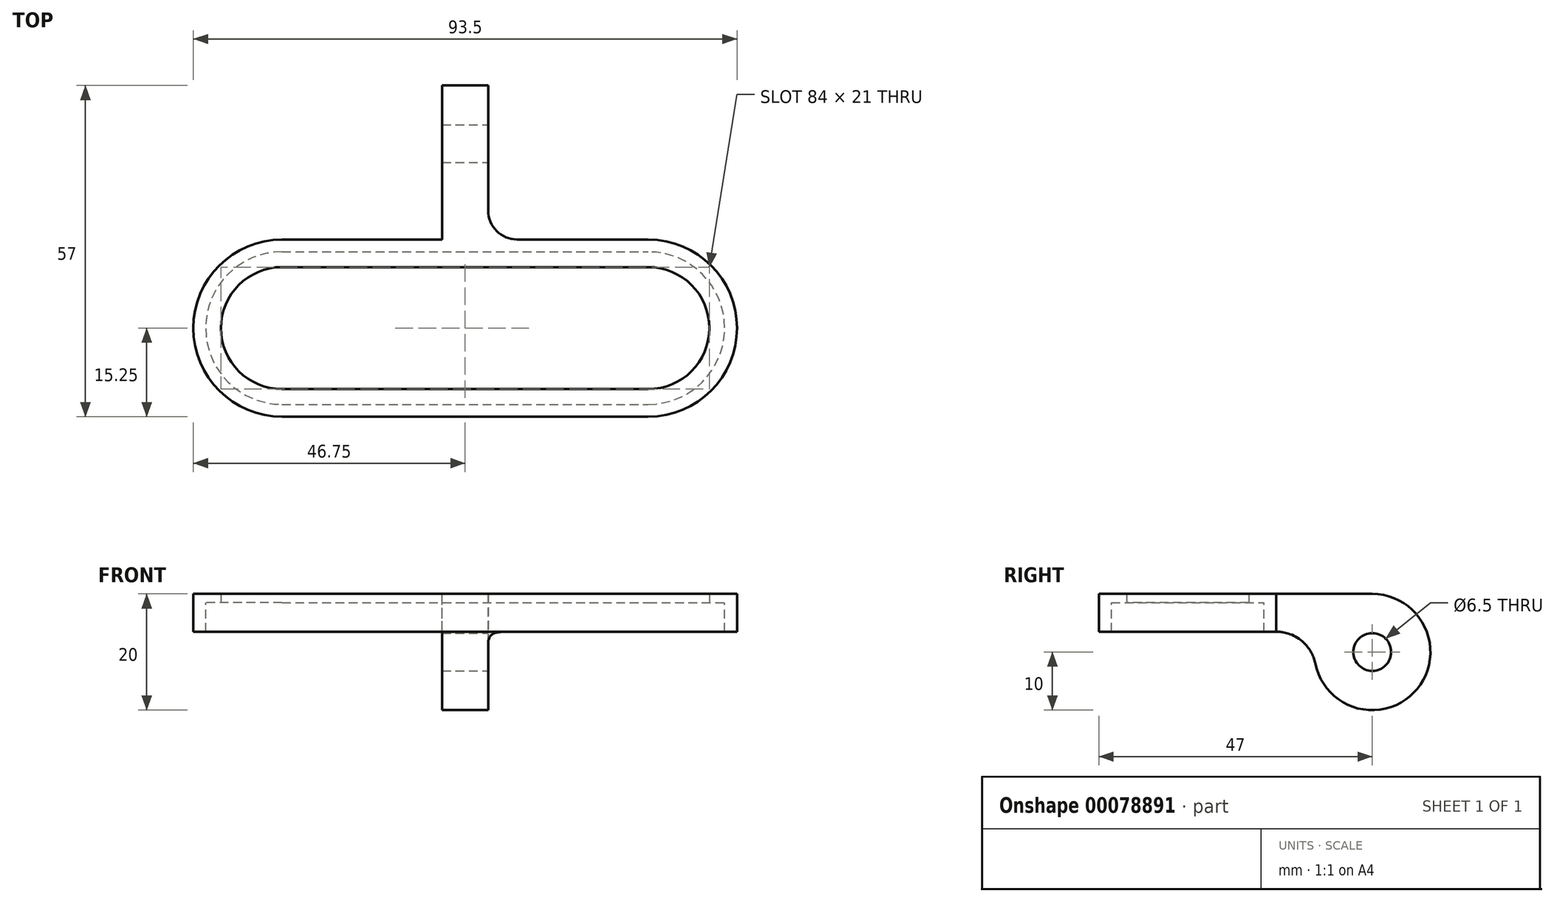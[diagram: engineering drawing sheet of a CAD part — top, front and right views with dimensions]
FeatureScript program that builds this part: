
annotation { "Feature Type Name" : "Feature", "Feature Type Description" : "" }
export const myFeature = defineFeature(function(context is Context, id is Id, definition is map)
    precondition{}
    {
        {
            var Q0;
            Q0=qCreatedBy(makeId("Top.planeOp"),FACE);
            var sketch = newSketch(context, id + "F0", { "sketchPlane" : qUnion([Q0])});
            skLineSegment(sketch, "E0", {"start": v(0, 0) * mm, "end": v(63, 0) * mm, "construction": true});
            skLineSegment(sketch, "E1", {"start": v(0, -25.5) * mm, "end": v(63, -25.5) * mm, "construction": true});
            skArc(sketch, "E2", {"start": v(0, -25.5) * mm, "mid": v(-12.75, -12.75) * mm, "end": v(0, 0) * mm, "construction": true});
            skArc(sketch, "E3", {"start": v(63, 0) * mm, "mid": v(75.75, -12.75) * mm, "end": v(63, -25.5) * mm, "construction": true});
            skArc(sketch, "E4.0", {"start": v(0, -23.25) * mm, "mid": v(-10.5, -12.75) * mm, "end": v(0, -2.25) * mm});
            skLineSegment(sketch, "E4.1", {"start": v(0, -23.25) * mm, "end": v(63, -23.25) * mm});
            skArc(sketch, "E4.2", {"start": v(63, -2.25) * mm, "mid": v(73.5, -12.75) * mm, "end": v(63, -23.25) * mm});
            skLineSegment(sketch, "E4.3", {"start": v(0, -2.25) * mm, "end": v(63, -2.25) * mm});
            skArc(sketch, "E5.0", {"start": v(0, -28) * mm, "mid": v(-15.25, -12.75) * mm, "end": v(0, 2.5) * mm});
            skLineSegment(sketch, "E5.1", {"start": v(0, -28) * mm, "end": v(63, -28) * mm});
            skArc(sketch, "E5.2", {"start": v(63, 2.5) * mm, "mid": v(78.25, -12.75) * mm, "end": v(63, -28) * mm});
            skLineSegment(sketch, "E5.3", {"start": v(0, 2.5) * mm, "end": v(63, 2.5) * mm});
            skSolve(sketch);
        }
        {
            var Q0;
            Q0 = qSketchRegion(id + "F0", true);
            extrude(context, id + "F1", {"entities" : qUnion([Q0]), "depth" : 1.5 * mm});
        }
        {
            var Q0;
            Q0=makeQuery(id+"F1.opExtrude","CAP_FACE",FACE,{"disambiguationData":[OSD([sQuery(id+"F0.wireOp",EDGE,"E4.0"),sQuery(id+"F0.wireOp",EDGE,"E4.1"),sQuery(id+"F0.wireOp",EDGE,"E4.2"),sQuery(id+"F0.wireOp",EDGE,"E4.3"),sQuery(id+"F0.wireOp",EDGE,"E5.0"),sQuery(id+"F0.wireOp",EDGE,"E5.1"),sQuery(id+"F0.wireOp",EDGE,"E5.2"),sQuery(id+"F0.wireOp",EDGE,"E5.3")])],"isStart":true});
            var sketch = newSketch(context, id + "F2", { "sketchPlane" : qUnion([Q0])});
            skArc(sketch, "E6.0", {"start": v(0, 25.88) * mm, "mid": v(-13.13, 12.75) * mm, "end": v(0, -0.38) * mm});
            skLineSegment(sketch, "E6.1", {"start": v(0, 25.88) * mm, "end": v(63, 25.88) * mm});
            skArc(sketch, "E6.2", {"start": v(63, -0.38) * mm, "mid": v(76.12, 12.75) * mm, "end": v(63, 25.88) * mm});
            skLineSegment(sketch, "E6.3", {"start": v(0, -0.38) * mm, "end": v(63, -0.38) * mm});
            skLineSegment(sketch, "E7", {"start": v(0, 28) * mm, "end": v(63, 28) * mm});
            skLineSegment(sketch, "E8", {"start": v(0, -2.5) * mm, "end": v(63, -2.5) * mm});
            skArc(sketch, "E9", {"start": v(63, 28) * mm, "mid": v(78.25, 12.75) * mm, "end": v(63, -2.5) * mm});
            skArc(sketch, "E10", {"start": v(0, 28) * mm, "mid": v(-15.25, 12.75) * mm, "end": v(0, -2.5) * mm});
            skSolve(sketch);
        }
        {
            var Q0;
            Q0 = qSketchRegion(id + "F2", true);
            extrude(context, id + "F3", {"entities" : qUnion([Q0]), "operationType" : NewBodyOperationType.ADD, "depth" : 5 * mm});
        }
        {
            var Q0;
            Q0=makeQuery(id+"F3.boolean.opBoolean","MERGE",FACE,{"derivedFrom":[makeQuery(id+"F1.opExtrude","SWEPT_FACE",FACE,{"disambiguationData":[OSD([sQuery(id+"F0.wireOp",EDGE,"E5.3")])]}),makeQuery(id+"F3.opExtrude","SWEPT_FACE",FACE,{"disambiguationData":[OSD([sQuery(id+"F2.wireOp",EDGE,"E8")])]})]});
            var sketch = newSketch(context, id + "F4", { "sketchPlane" : qUnion([Q0])});
            skLineSegment(sketch, "E11", {"start": v(-31.5, -18.5) * mm, "end": v(-31.5, 1.5) * mm, "construction": true});
            skPoint(sketch, "E11.endSnap0", {"position": v(-31.5, 1.5) * mm});
            skLineSegment(sketch, "E12", {"start": v(-27.55, -18.5) * mm, "end": v(-27.55, 1.5) * mm});
            skLineSegment(sketch, "E13", {"start": v(-27.55, 1.5) * mm, "end": v(-35.45, 1.5) * mm});
            skLineSegment(sketch, "E14", {"start": v(-35.45, 1.5) * mm, "end": v(-35.45, -18.5) * mm});
            skLineSegment(sketch, "E15", {"start": v(-35.45, -18.5) * mm, "end": v(-27.55, -18.5) * mm});
            skLineSegment(sketch, "E16", {"start": v(0, -1.75) * mm, "end": v(-63, -1.75) * mm, "construction": true});
            skLineSegment(sketch, "E17", {"start": v(-27.55, -8.5) * mm, "end": v(-35.45, -8.5) * mm, "construction": true});
            skSolve(sketch);
        }
        {
            var Q0;
            Q0 = qSketchRegion(id + "F4", true);
            extrude(context, id + "F5", {"entities" : qUnion([Q0]), "operationType" : NewBodyOperationType.ADD, "depth" : 26.5 * mm});
        }
        {
            var Q0;
            Q0=makeQuery(id+"F5.opExtrude","SWEPT_FACE",FACE,{"disambiguationData":[OSD([sQuery(id+"F4.wireOp",EDGE,"E14")])]});
            var sketch = newSketch(context, id + "F6", { "sketchPlane" : qUnion([Q0])});
            skLineSegment(sketch, "E18", {"start": v(2.5, -5) * mm, "end": v(0.38, -5) * mm});
            skLineSegment(sketch, "E19", {"start": v(2.5, -5) * mm, "end": v(2.5, -7.12) * mm});
            skArc(sketch, "E20", {"start": v(2.5, -7.12) * mm, "mid": v(1.88, -5.62) * mm, "end": v(0.38, -5) * mm});
            skSolve(sketch);
        }
        {
            var Q0;
            Q0=makeQuery(id+"FXbGKdrpCwlS0YJ_1.boolean.opBoolean","MERGE",FACE,{"derivedFrom":[makeQuery(id+"F5.opExtrude","SWEPT_FACE",FACE,{"disambiguationData":[OSD([sQuery(id+"F4.wireOp",EDGE,"E14")])]}),makeQuery(id+"FXbGKdrpCwlS0YJ_1.opExtrude","CAP_FACE",FACE,{"disambiguationData":[OSD([sQuery(id+"F6.wireOp",EDGE,"E18"),sQuery(id+"F6.wireOp",EDGE,"E19"),sQuery(id+"F6.wireOp",EDGE,"E20")])],"isStart":true})]});
            var sketch = newSketch(context, id + "F7", { "sketchPlane" : qUnion([Q0])});
            skLineSegment(sketch, "E21", {"start": v(29, -18.5) * mm, "end": v(19, -18.5) * mm, "construction": true});
            skLineSegment(sketch, "E22", {"start": v(29, -8.5) * mm, "end": v(41.92, -8.5) * mm, "construction": true});
            skLineSegment(sketch, "E23", {"start": v(29, -8.5) * mm, "end": v(29, -18.5) * mm, "construction": true});
            skLineSegment(sketch, "E24", {"start": v(29, -8.5) * mm, "end": v(29, 1.5) * mm, "construction": true});
            skLineSegment(sketch, "E25", {"start": v(29, 1.5) * mm, "end": v(19, 1.5) * mm, "construction": true});
            skLineSegment(sketch, "E26", {"start": v(-1.5, -23.8) * mm, "end": v(36.26, -23.8) * mm});
            skLineSegment(sketch, "E27", {"start": v(36.26, -23.8) * mm, "end": v(36.26, 7.74) * mm});
            skLineSegment(sketch, "E28", {"start": v(36.26, 7.74) * mm, "end": v(19, 7.74) * mm});
            skLineSegment(sketch, "E29", {"start": v(19, 7.74) * mm, "end": v(19, 1.5) * mm});
            skArc(sketch, "E30", {"start": v(19, -18.5) * mm, "mid": v(29, -8.5) * mm, "end": v(19, 1.5) * mm});
            skCircle(sketch, "E31", {"center": v(19, -8.5) * mm, "radius": 3.25 * mm});
            skArc(sketch, "E32", {"start": v(19, -18.5) * mm, "mid": v(12.67, -16.24) * mm, "end": v(9.2, -10.48) * mm});
            skArc(sketch, "E33", {"start": v(9.2, -10.48) * mm, "mid": v(6.83, -6.54) * mm, "end": v(2.5, -5) * mm});
            skLineSegment(sketch, "E34", {"start": v(-1.5, -23.8) * mm, "end": v(-1.5, -8.44) * mm});
            skLineSegment(sketch, "E35", {"start": v(-1.5, -8.44) * mm, "end": v(2.5, -5) * mm});
            skSolve(sketch);
        }
        {
            var Q0;
            Q0 = qSketchRegion(id + "F7", true);
            extrude(context, id + "F8", {"entities" : qUnion([Q0]), "operationType" : NewBodyOperationType.REMOVE, "endBound" : BoundingType.THROUGH_ALL, "oppositeDirection" : true, "depth" : 25 * mm});
        }
        {
            var Q0;
            {var subQ1=sQuery(id+"F4.wireOp",EDGE,"E13");var subQ3=sQuery(id+"F4.wireOp",EDGE,"E14");Q0=makeQuery(id+"F5.boolean.opBoolean","SPLIT",EDGE,{"disambiguationData":[TD([makeQuery(id+"F5.opExtrude","SWEPT_FACE",FACE,{"disambiguationData":[OSD([subQ1])]})])],"derivedFrom":makeQuery(id+"F5.opExtrude","CAP_EDGE",EDGE,{"disambiguationData":[OSD([subQ3])],"isStart":true})});}
            var Q1;
            {var subQ1=sQuery(id+"F4.wireOp",EDGE,"E13");var subQ3=sQuery(id+"F4.wireOp",EDGE,"E12");Q1=makeQuery(id+"F5.boolean.opBoolean","SPLIT",EDGE,{"disambiguationData":[TD([makeQuery(id+"F5.opExtrude","SWEPT_FACE",FACE,{"disambiguationData":[OSD([subQ1])]})])],"derivedFrom":makeQuery(id+"F5.opExtrude","CAP_EDGE",EDGE,{"disambiguationData":[OSD([subQ3])],"isStart":true})});}
            fillet(context, id + "F9", {"entities" : qUnion([Q0, Q1]), "radius" : 5 * mm, "tangentPropagation" : true, "allowEdgeOverflow" : false});
        }
    });
